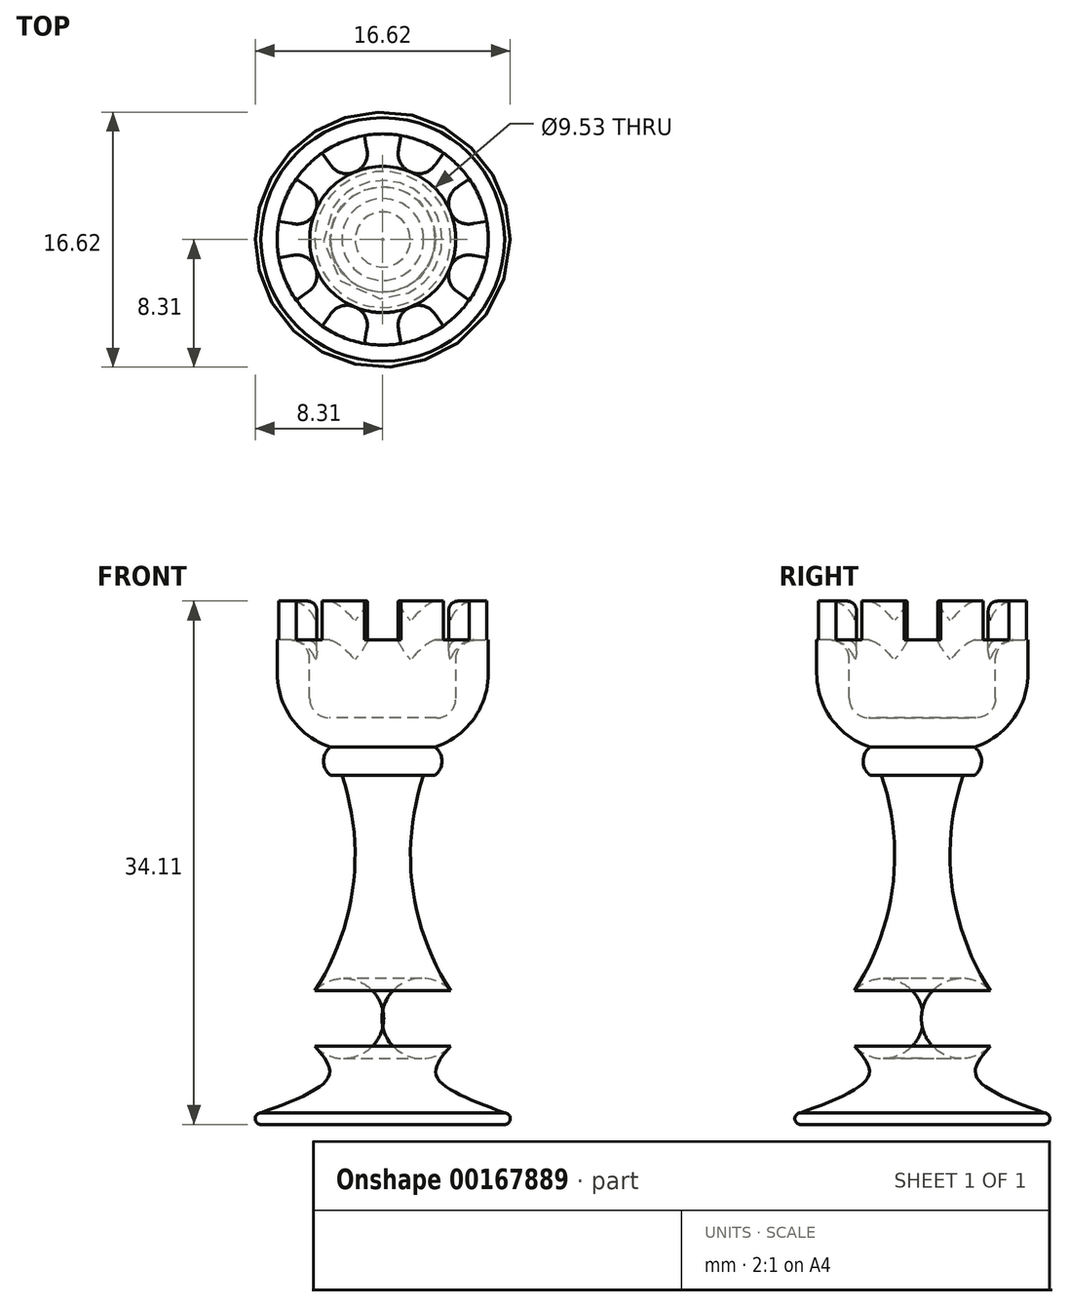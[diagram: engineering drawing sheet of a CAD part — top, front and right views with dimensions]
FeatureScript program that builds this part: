
annotation { "Feature Type Name" : "Feature", "Feature Type Description" : "" }
export const myFeature = defineFeature(function(context is Context, id is Id, definition is map)
    precondition{}
    {
        {
            var Q0;
            Q0=qCreatedBy(makeId("Front.planeOp"),FACE);
            var sketch = newSketch(context, id + "F0", { "sketchPlane" : qUnion([Q0])});
            skLineSegment(sketch, "E0", {"start": v(0, 24.58) * mm, "end": v(0, 0) * mm});
            skLineSegment(sketch, "E1", {"start": v(0, 0) * mm, "end": v(7.94, 0) * mm});
            skArc(sketch, "E2", {"start": v(2.67, 22.76) * mm, "mid": v(1.93, 15.54) * mm, "end": v(4.43, 8.71) * mm});
            skArc(sketch, "E3", {"start": v(4.43, 5.1) * mm, "mid": v(5.16, 6.9) * mm, "end": v(4.43, 8.71) * mm});
            skArc(sketch, "E4", {"start": v(3.4, 22.76) * mm, "mid": v(3.86, 23.67) * mm, "end": v(3.4, 24.58) * mm});
            skLineSegment(sketch, "E5", {"start": v(3.4, 22.76) * mm, "end": v(2.67, 22.76) * mm});
            skArc(sketch, "E6", {"start": v(7.94, 0) * mm, "mid": v(8.31, 0.38) * mm, "end": v(7.94, 0.75) * mm});
            skFitSpline(sketch, "E7", {"points": [v(4.43, 5.1) * mm, v(3.48, 3.2) * mm, v(7.94, 0.75) * mm], "startDerivative": vector(-4.32, -4.97) * mm, "endDerivative": vector(10.28, -3.8) * mm});
            skLineSegment(sketch, "E8", {"start": v(3.4, 24.58) * mm, "end": v(0, 24.58) * mm});
            skPoint(sketch, "E9.end.orphan", {"position": v(3.4, 38.1) * mm});
            skPoint(sketch, "E10.orphan", {"position": v(0, 38.1) * mm});
            skSolve(sketch);
        }
        {
            var Q0;
            Q0=qSketchRegion(id+"F0",true);
            var Q1;
            Q1=sQuery(id+"F0.wireOp",EDGE,"E0");
            revolve(context, id + "F1", {"entities" : qUnion([Q0]), "axis" : qUnion([Q1]), "revolveType" : RevolveType.FULL});
        }
        {
            var Q0;
            Q0=makeQuery(id+"F1.opRevolve","SWEPT_FACE",FACE,{"disambiguationData":[OSD([sQuery(id+"F0.wireOp",EDGE,"E8")])]});
            var sketch = newSketch(context, id + "F2", { "sketchPlane" : qUnion([Q0])});
            skCircle(sketch, "E11", {"center": v(0, 0) * mm, "radius": 6.88 * mm});
            skSolve(sketch);
        }
        {
            var Q0;
            Q0 = qSketchRegion(id + "F2", true);
            extrude(context, id + "F3", {"entities" : qUnion([Q0]), "operationType" : NewBodyOperationType.ADD, "depth" : 9.52 * mm});
        }
        {
            var Q0;
            Q0=makeQuery(id+"F3.opExtrude","CAP_FACE",FACE,{"disambiguationData":[OSD([sQuery(id+"F2.wireOp",EDGE,"E11")])],"isStart":false});
            var sketch = newSketch(context, id + "F4", { "sketchPlane" : qUnion([Q0])});
            skCircle(sketch, "E12", {"center": v(0, 0) * mm, "radius": 4.76 * mm});
            skSolve(sketch);
        }
        {
            var Q0;
            Q0 = qSketchRegion(id + "F4", true);
            extrude(context, id + "F5", {"entities" : qUnion([Q0]), "operationType" : NewBodyOperationType.REMOVE, "oppositeDirection" : true, "depth" : 7.62 * mm});
        }
        {
            var Q0;
            Q0=makeQuery(id+"F3.opExtrude","CAP_FACE",FACE,{"disambiguationData":[OSD([sQuery(id+"F2.wireOp",EDGE,"E11")])],"isStart":false});
            var sketch = newSketch(context, id + "F6", { "sketchPlane" : qUnion([Q0])});
            skLineSegment(sketch, "E13", {"start": v(4.7, 0.83) * mm, "end": v(6.78, 1.2) * mm});
            skLineSegment(sketch, "E14.MirrorCS", {"start": v(4.7, -0.83) * mm, "end": v(6.78, -1.2) * mm});
            skCircle(sketch, "E15.0.0", {"center": v(0, 0) * mm, "radius": 6.88 * mm});
            skPoint(sketch, "E16.orphan", {"position": v(10.28, -1.81) * mm});
            skCircle(sketch, "E17.0", {"center": v(0, 0) * mm, "radius": 4.76 * mm});
            skLineSegment(sketch, "E18.1.0", {"start": v(2.73, 3.9) * mm, "end": v(3.95, 5.64) * mm});
            skLineSegment(sketch, "E18.1.1", {"start": v(3.9, 2.73) * mm, "end": v(5.64, 3.95) * mm});
            skLineSegment(sketch, "E18.2.0", {"start": v(-0.83, 4.7) * mm, "end": v(-1.2, 6.78) * mm});
            skLineSegment(sketch, "E18.2.1", {"start": v(0.83, 4.7) * mm, "end": v(1.2, 6.78) * mm});
            skLineSegment(sketch, "E18.3.0", {"start": v(-3.9, 2.73) * mm, "end": v(-5.64, 3.95) * mm});
            skLineSegment(sketch, "E18.3.1", {"start": v(-2.73, 3.9) * mm, "end": v(-3.95, 5.64) * mm});
            skLineSegment(sketch, "E18.4.0", {"start": v(-4.7, -0.83) * mm, "end": v(-6.78, -1.2) * mm});
            skLineSegment(sketch, "E18.4.1", {"start": v(-4.7, 0.83) * mm, "end": v(-6.78, 1.2) * mm});
            skLineSegment(sketch, "E18.5.0", {"start": v(-2.73, -3.9) * mm, "end": v(-3.95, -5.64) * mm});
            skLineSegment(sketch, "E18.5.1", {"start": v(-3.9, -2.73) * mm, "end": v(-5.64, -3.95) * mm});
            skLineSegment(sketch, "E18.6.0", {"start": v(0.83, -4.7) * mm, "end": v(1.2, -6.78) * mm});
            skLineSegment(sketch, "E18.6.1", {"start": v(-0.83, -4.7) * mm, "end": v(-1.2, -6.78) * mm});
            skLineSegment(sketch, "E19.1.7.0", {"start": v(3.9, -2.73) * mm, "end": v(5.64, -3.95) * mm});
            skLineSegment(sketch, "E19.3.7.0", {"start": v(2.73, -3.9) * mm, "end": v(3.95, -5.64) * mm});
            skSolve(sketch);
        }
        {
            var Q0;
            {var subQ0=sQuery(id+"F6.wireOp",EDGE,"E13");Q0=makeQuery(id+"F6.imprint","IMPRINT",FACE,{"disambiguationData":[TD([[makeQuery(id+"F6.imprint","IMPRINT",EDGE,{"derivedFrom":subQ0}),-1.0]])]});}
            var Q1;
            {var subQ0=sQuery(id+"F6.wireOp",EDGE,"E18.1.0");Q1=makeQuery(id+"F6.imprint","IMPRINT",FACE,{"disambiguationData":[TD([[makeQuery(id+"F6.imprint","IMPRINT",EDGE,{"derivedFrom":subQ0}),-1.0]])]});}
            var Q2;
            {var subQ0=sQuery(id+"F6.wireOp",EDGE,"E18.2.0");Q2=makeQuery(id+"F6.imprint","IMPRINT",FACE,{"disambiguationData":[TD([[makeQuery(id+"F6.imprint","IMPRINT",EDGE,{"derivedFrom":subQ0}),-1.0]])]});}
            var Q3;
            {var subQ0=sQuery(id+"F6.wireOp",EDGE,"E18.3.0");Q3=makeQuery(id+"F6.imprint","IMPRINT",FACE,{"disambiguationData":[TD([[makeQuery(id+"F6.imprint","IMPRINT",EDGE,{"derivedFrom":subQ0}),-1.0]])]});}
            var Q4;
            {var subQ0=sQuery(id+"F6.wireOp",EDGE,"E18.4.0");Q4=makeQuery(id+"F6.imprint","IMPRINT",FACE,{"disambiguationData":[TD([[makeQuery(id+"F6.imprint","IMPRINT",EDGE,{"derivedFrom":subQ0}),-1.0]])]});}
            var Q5;
            {var subQ0=sQuery(id+"F6.wireOp",EDGE,"E18.5.0");Q5=makeQuery(id+"F6.imprint","IMPRINT",FACE,{"disambiguationData":[TD([[makeQuery(id+"F6.imprint","IMPRINT",EDGE,{"derivedFrom":subQ0}),-1.0]])]});}
            var Q6;
            {var subQ0=sQuery(id+"F6.wireOp",EDGE,"E18.6.0");Q6=makeQuery(id+"F6.imprint","IMPRINT",FACE,{"disambiguationData":[TD([[makeQuery(id+"F6.imprint","IMPRINT",EDGE,{"derivedFrom":subQ0}),-1.0]])]});}
            var Q7;
            {var subQ0=sQuery(id+"F6.wireOp",EDGE,"E19.1.7.0");Q7=makeQuery(id+"F6.imprint","IMPRINT",FACE,{"disambiguationData":[TD([[makeQuery(id+"F6.imprint","IMPRINT",EDGE,{"derivedFrom":subQ0}),-1.0]])]});}
            extrude(context, id + "F7", {"entities" : qUnion([Q0, Q1, Q2, Q3, Q4, Q5, Q6, Q7]), "operationType" : NewBodyOperationType.REMOVE, "oppositeDirection" : true, "depth" : 2.54 * mm});
        }
        {
            var Q0;
            Q0=makeQuery(id+"F3.opExtrude","CAP_EDGE",EDGE,{"disambiguationData":[OSD([sQuery(id+"F2.wireOp",EDGE,"E11")])],"isStart":true});
            fillet(context, id + "F8", {"entities" : qUnion([Q0]), "radius" : 5.08 * mm, "tangentPropagation" : true, "allowEdgeOverflow" : false});
        }
        {
            var Q0;
            Q0=makeQuery(id+"F5.boolean.opBoolean","COPY",FACE,{"derivedFrom":makeQuery(id+"F5.opExtrude","SWEPT_FACE",FACE,{"disambiguationData":[OSD([sQuery(id+"F4.wireOp",EDGE,"E12")])]})});
            fillet(context, id + "F9", {"entities" : qUnion([Q0]), "radius" : 1.27 * mm, "tangentPropagation" : true, "allowEdgeOverflow" : false});
        }
    });
